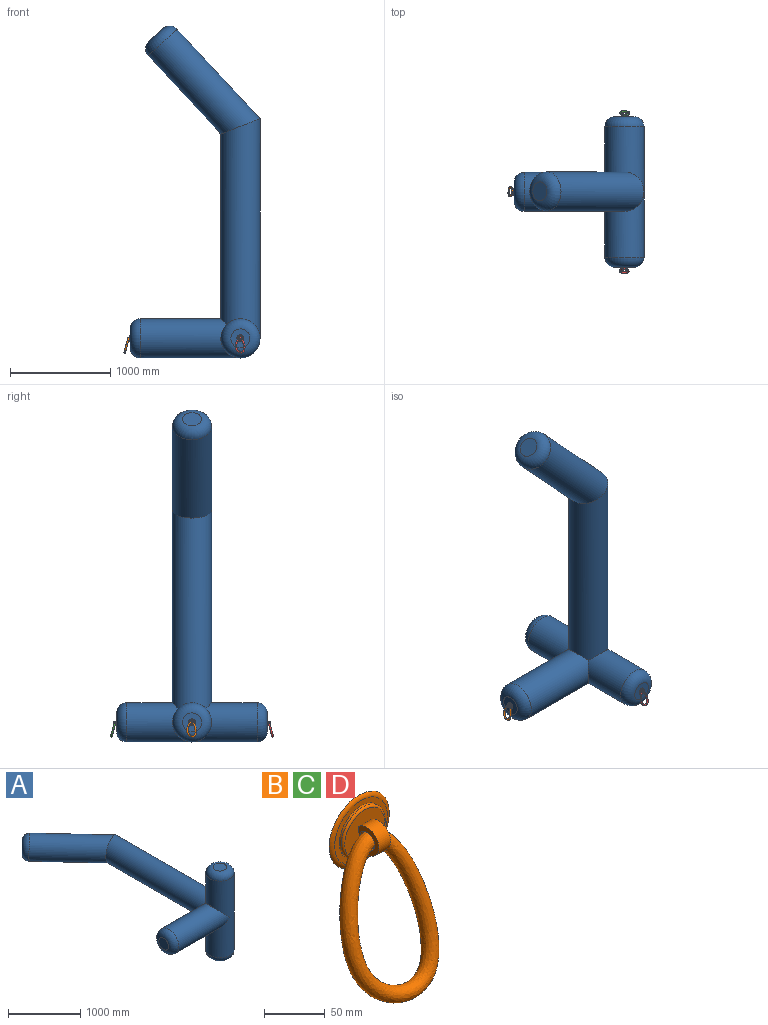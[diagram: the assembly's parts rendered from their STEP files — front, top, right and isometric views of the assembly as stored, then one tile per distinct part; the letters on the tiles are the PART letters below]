
ASSEMBLY  parts=4 mates=3
PART A: 12 faces, bbox 1295x3339.8x1500 mm
  f0: plane 190x139.3mm, normal (-0.68,0.73,0), area 28352.9mm2, adj f11
  f1: cylinder r=195mm len=1157.16mm, axis (-0.68,0.73,0), area 1396753.5mm2, adj f2,f11
  f2: cylinder r=195mm len=2190.55mm, axis (0,1,0), area 2406517.9mm2, adj f1,f5,f7
  f3: plane 190x190mm, normal (0,0,-1), area 28352.9mm2, adj f10
  f4: plane 190x190mm, normal (0,0,1), area 28352.9mm2, adj f9
  f5: cylinder r=195mm len=1300mm, axis (0,0,1), area 1333136.6mm2, adj f2,f7,f9,f10
  f6: plane 190x190mm, normal (-1,0,0), area 28352.9mm2, adj f8
  f7: cylinder r=195mm len=1000mm, axis (-1,0,0), area 1041620.2mm2, adj f2,f5,f8
  f8: torus R=95mm, axis (1,0,0), area 156593.1mm2, adj f6,f7
  f9: torus R=95mm, axis (0,0,1), area 156593.1mm2, adj f4,f5
  f10: torus R=95mm, axis (0,0,1), area 156593.1mm2, adj f3,f5
  f11: torus R=95mm, axis (0.68,-0.73,0), area 156593.1mm2, adj f0,f1
PART B: 11 faces, bbox 98.3x63.5x184.6 mm
  f0: plane 61.58x61.58mm, normal (0,-1,0), area 978.4mm2, adj f2,f3
  f1: plane 70x70mm, normal (0,1,0), area 3848.5mm2, adj f2
  f2: torus R=30.79mm, axis (0,1,0), area 1040mm2, adj f0,f1
  f3: cylinder r=25.23mm len=50.47mm, axis (0,1,0), area 348.8mm2, adj f0,f5
  f4: plane 46.47x46.47mm, normal (0,-1,0), area 1427.9mm2, adj f5,f7,f8,f9
  f5: torus R=23.23mm, axis (0,-1,0), area 483.7mm2, adj f3,f4
  f6: cylinder r=8.84mm len=17.69mm, axis (-1,0,0), area 693.6mm2, adj f8,f9,f10
  f7: cylinder r=13.83mm len=27.66mm, axis (-1,0,0), area 883.8mm2, adj f4,f8,f9
  f8: plane 27.66x23.54mm, normal (1,0,0), area 250mm2, adj f4,f6,f7,f10
  f9: plane 27.66x23.54mm, normal (-1,0,0), area 299.3mm2, adj f4,f6,f7
  f10: bspline ~153.47x98.35mm, area 16858.8mm2, adj f6,f8
PART C: same geometry as B
PART D: same geometry as B
PLACE A rot(axis=(1,0,0),90deg) t=(0,0,195)mm
PLACE B rot(axis=(0,0,-1),90deg) t=(-1100,0,195)mm
PLACE C rot(axis=(0,0,1),180deg) t=(0,750,195)mm
PLACE D t=(0,-750,195)mm
MATE fastened B.f2 <-> A.f7  axis (1,0,0) through (-1100,0,195)mm
MATE fastened D.f2 <-> A.f5  axis (0,1,0) through (0,-750,195)mm
MATE fastened C.f2 <-> A.f5  axis (0,-1,0) through (0,750,195)mm
